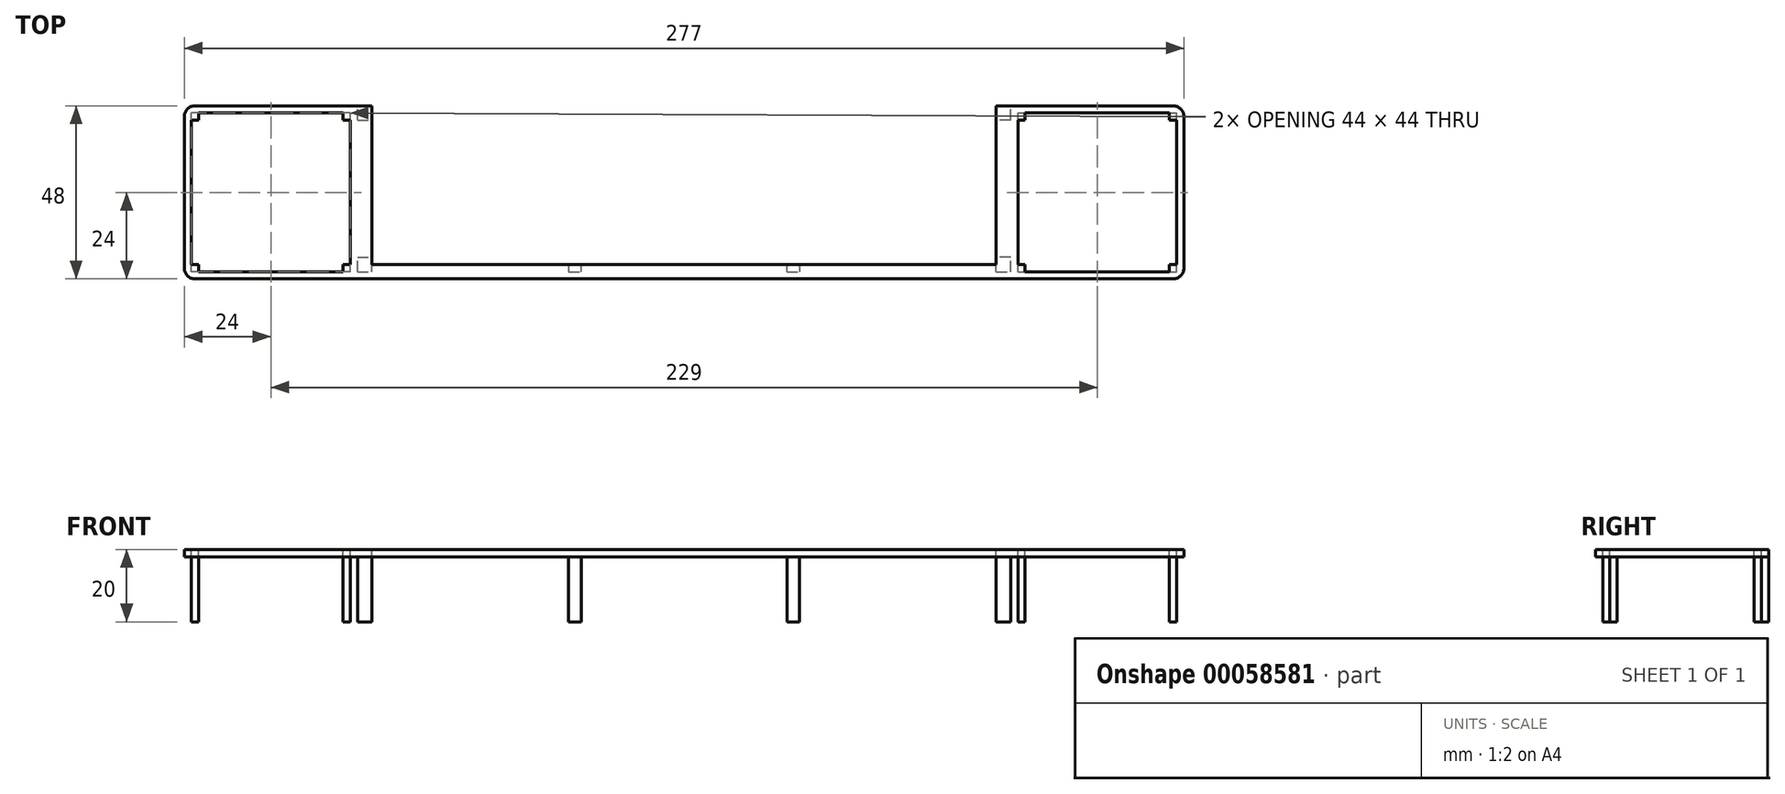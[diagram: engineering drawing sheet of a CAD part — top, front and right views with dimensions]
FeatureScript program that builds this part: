
annotation { "Feature Type Name" : "Feature", "Feature Type Description" : "" }
export const myFeature = defineFeature(function(context is Context, id is Id, definition is map)
    precondition{}
    {
        {
            var Q0;
            Q0=qCreatedBy(makeId("Top.planeOp"),FACE);
            var sketch = newSketch(context, id + "F0", { "sketchPlane" : qUnion([Q0])});
            skLineSegment(sketch, "E0", {"start": v(0, 42.64) * mm, "end": v(0, 0) * mm, "construction": true});
            skLineSegment(sketch, "E1", {"start": v(0, 0) * mm, "end": v(-90.5, 0) * mm, "construction": true});
            skLineSegment(sketch, "E2.bottom", {"start": v(-90.5, 0) * mm, "end": v(-138.5, 0) * mm});
            skLineSegment(sketch, "E2.top", {"start": v(-90.5, 48) * mm, "end": v(-138.5, 48) * mm});
            skLineSegment(sketch, "E2.left", {"start": v(-90.5, 2) * mm, "end": v(-90.5, 48) * mm});
            skLineSegment(sketch, "E2.right", {"start": v(-138.5, 0) * mm, "end": v(-138.5, 48) * mm});
            skLineSegment(sketch, "E3.0", {"start": v(-92.5, 46) * mm, "end": v(-136.5, 46) * mm});
            skLineSegment(sketch, "E3.1", {"start": v(-92.5, 2) * mm, "end": v(-92.5, 46) * mm});
            skLineSegment(sketch, "E3.2", {"start": v(-92.5, 2) * mm, "end": v(-136.5, 2) * mm});
            skLineSegment(sketch, "E3.3", {"start": v(-136.5, 2) * mm, "end": v(-136.5, 46) * mm});
            skLineSegment(sketch, "E4", {"start": v(-90.5, 0) * mm, "end": v(0, 0) * mm});
            skLineSegment(sketch, "E5", {"start": v(-90.5, 2) * mm, "end": v(0, 2) * mm});
            skLineSegment(sketch, "E6", {"start": v(0, 0) * mm, "end": v(0, 2) * mm});
            skSolve(sketch);
        }
        {
            var Q0;
            Q0 = qSketchRegion(id + "F0", true);
            extrude(context, id + "F1", {"entities" : qUnion([Q0]), "depth" : 17 * mm});
        }
        {
            var Q0;
            Q0=makeQuery(id+"F1.opExtrude","CAP_FACE",FACE,{"disambiguationData":[OSD([sQuery(id+"F0.wireOp",EDGE,"E2.bottom"),sQuery(id+"F0.wireOp",EDGE,"E2.top"),sQuery(id+"F0.wireOp",EDGE,"E2.left"),sQuery(id+"F0.wireOp",EDGE,"E2.right"),sQuery(id+"F0.wireOp",EDGE,"E3.0"),sQuery(id+"F0.wireOp",EDGE,"E3.1"),sQuery(id+"F0.wireOp",EDGE,"E3.2"),sQuery(id+"F0.wireOp",EDGE,"E3.3"),sQuery(id+"F0.wireOp",EDGE,"E4"),sQuery(id+"F0.wireOp",EDGE,"E5"),sQuery(id+"F0.wireOp",EDGE,"8706801c-66d0-493c-a020-fb1d76b9bbb51.MirrorCS"),sQuery(id+"F0.wireOp",EDGE,"8706801c-66d0-493c-a020-fb1d76b9bbb52.MirrorCS"),sQuery(id+"F0.wireOp",EDGE,"8706801c-66d0-493c-a020-fb1d76b9bbb53.MirrorCS"),sQuery(id+"F0.wireOp",EDGE,"8706801c-66d0-493c-a020-fb1d76b9bbb54.MirrorCS"),sQuery(id+"F0.wireOp",EDGE,"8706801c-66d0-493c-a020-fb1d76b9bbb55.MirrorCS"),sQuery(id+"F0.wireOp",EDGE,"8706801c-66d0-493c-a020-fb1d76b9bbb56.MirrorCS"),sQuery(id+"F0.wireOp",EDGE,"8706801c-66d0-493c-a020-fb1d76b9bbb57.MirrorCS"),sQuery(id+"F0.wireOp",EDGE,"8706801c-66d0-493c-a020-fb1d76b9bbb58.MirrorCS"),sQuery(id+"F0.wireOp",EDGE,"8706801c-66d0-493c-a020-fb1d76b9bbb59.MirrorCS"),sQuery(id+"F0.wireOp",EDGE,"8706801c-66d0-493c-a020-fb1d76b9bbb510.MirrorCS")])],"isStart":false});
            var sketch = newSketch(context, id + "F2", { "sketchPlane" : qUnion([Q0])});
            skLineSegment(sketch, "E7.bottom", {"start": v(-136.5, 2) * mm, "end": v(-134.5, 2) * mm});
            skLineSegment(sketch, "E7.top", {"start": v(-136.5, 4) * mm, "end": v(-134.5, 4) * mm});
            skLineSegment(sketch, "E7.left", {"start": v(-136.5, 2) * mm, "end": v(-136.5, 4) * mm});
            skLineSegment(sketch, "E7.right", {"start": v(-134.5, 2) * mm, "end": v(-134.5, 4) * mm});
            skLineSegment(sketch, "E8.bottom", {"start": v(-136.5, 46) * mm, "end": v(-134.5, 46) * mm});
            skLineSegment(sketch, "E8.top", {"start": v(-136.5, 44) * mm, "end": v(-134.5, 44) * mm});
            skLineSegment(sketch, "E8.left", {"start": v(-136.5, 46) * mm, "end": v(-136.5, 44) * mm});
            skLineSegment(sketch, "E8.right", {"start": v(-134.5, 46) * mm, "end": v(-134.5, 44) * mm});
            skLineSegment(sketch, "E9.bottom", {"start": v(-92.5, 2) * mm, "end": v(-94.5, 2) * mm});
            skLineSegment(sketch, "E9.top", {"start": v(-92.5, 4) * mm, "end": v(-94.5, 4) * mm});
            skLineSegment(sketch, "E9.left", {"start": v(-92.5, 2) * mm, "end": v(-92.5, 4) * mm});
            skLineSegment(sketch, "E9.right", {"start": v(-94.5, 2) * mm, "end": v(-94.5, 4) * mm});
            skLineSegment(sketch, "E10.bottom", {"start": v(-92.5, 46) * mm, "end": v(-94.5, 46) * mm});
            skLineSegment(sketch, "E10.top", {"start": v(-92.5, 44) * mm, "end": v(-94.5, 44) * mm});
            skLineSegment(sketch, "E10.left", {"start": v(-92.5, 46) * mm, "end": v(-92.5, 44) * mm});
            skLineSegment(sketch, "E10.right", {"start": v(-94.5, 46) * mm, "end": v(-94.5, 44) * mm});
            skLineSegment(sketch, "E11.bottom", {"start": v(-90.5, 48) * mm, "end": v(-86.5, 48) * mm});
            skLineSegment(sketch, "E11.top", {"start": v(-90.5, 44) * mm, "end": v(-86.5, 44) * mm});
            skLineSegment(sketch, "E11.left", {"start": v(-90.5, 48) * mm, "end": v(-90.5, 44) * mm});
            skLineSegment(sketch, "E11.right", {"start": v(-86.5, 48) * mm, "end": v(-86.5, 44) * mm});
            skLineSegment(sketch, "E12.bottom", {"start": v(-90.5, 2) * mm, "end": v(-86.5, 2) * mm});
            skLineSegment(sketch, "E12.top", {"start": v(-90.5, 6) * mm, "end": v(-86.5, 6) * mm});
            skLineSegment(sketch, "E12.left", {"start": v(-90.5, 2) * mm, "end": v(-90.5, 6) * mm});
            skLineSegment(sketch, "E12.right", {"start": v(-86.5, 2) * mm, "end": v(-86.5, 6) * mm});
            skLineSegment(sketch, "E13.bottom", {"start": v(-32, 2) * mm, "end": v(-28.5, 2) * mm});
            skLineSegment(sketch, "E14", {"start": v(-32, 2) * mm, "end": v(-32, 4) * mm});
            skLineSegment(sketch, "E15", {"start": v(-32, 4) * mm, "end": v(-28.5, 4) * mm});
            skLineSegment(sketch, "E16", {"start": v(-28.5, 4) * mm, "end": v(-28.5, 2) * mm});
            skSolve(sketch);
        }
        {
            var Q0;
            Q0 = qSketchRegion(id + "F2", true);
            extrude(context, id + "F3", {"entities" : qUnion([Q0]), "operationType" : NewBodyOperationType.ADD, "oppositeDirection" : true, "depth" : 20 * mm});
        }
        {
            var Q0;
            Q0=makeQuery(id+"F3.boolean.opBoolean","MERGE",FACE,{"derivedFrom":[makeQuery(id+"F1.opExtrude","CAP_FACE",FACE,{"disambiguationData":[OSD([sQuery(id+"F0.wireOp",EDGE,"E2.bottom"),sQuery(id+"F0.wireOp",EDGE,"E2.top"),sQuery(id+"F0.wireOp",EDGE,"E2.left"),sQuery(id+"F0.wireOp",EDGE,"E2.right"),sQuery(id+"F0.wireOp",EDGE,"E3.0"),sQuery(id+"F0.wireOp",EDGE,"E3.1"),sQuery(id+"F0.wireOp",EDGE,"E3.2"),sQuery(id+"F0.wireOp",EDGE,"E3.3"),sQuery(id+"F0.wireOp",EDGE,"E4"),sQuery(id+"F0.wireOp",EDGE,"E5"),sQuery(id+"F0.wireOp",EDGE,"E6")])],"isStart":false}),makeQuery(id+"F3.opExtrude","CAP_FACE",FACE,{"disambiguationData":[OSD([sQuery(id+"F2.wireOp",EDGE,"E7.bottom"),sQuery(id+"F2.wireOp",EDGE,"E7.top"),sQuery(id+"F2.wireOp",EDGE,"E7.left"),sQuery(id+"F2.wireOp",EDGE,"E7.right")])],"isStart":true}),makeQuery(id+"F3.opExtrude","CAP_FACE",FACE,{"disambiguationData":[OSD([sQuery(id+"F2.wireOp",EDGE,"E8.bottom"),sQuery(id+"F2.wireOp",EDGE,"E8.top"),sQuery(id+"F2.wireOp",EDGE,"E8.left"),sQuery(id+"F2.wireOp",EDGE,"E8.right")])],"isStart":true}),makeQuery(id+"F3.opExtrude","CAP_FACE",FACE,{"disambiguationData":[OSD([sQuery(id+"F2.wireOp",EDGE,"E9.bottom"),sQuery(id+"F2.wireOp",EDGE,"E9.top"),sQuery(id+"F2.wireOp",EDGE,"E9.left"),sQuery(id+"F2.wireOp",EDGE,"E9.right")])],"isStart":true}),makeQuery(id+"F3.opExtrude","CAP_FACE",FACE,{"disambiguationData":[OSD([sQuery(id+"F2.wireOp",EDGE,"E10.bottom"),sQuery(id+"F2.wireOp",EDGE,"E10.top"),sQuery(id+"F2.wireOp",EDGE,"E10.left"),sQuery(id+"F2.wireOp",EDGE,"E10.right")])],"isStart":true}),makeQuery(id+"F3.opExtrude","CAP_FACE",FACE,{"disambiguationData":[OSD([sQuery(id+"F2.wireOp",EDGE,"E11.bottom"),sQuery(id+"F2.wireOp",EDGE,"E11.top"),sQuery(id+"F2.wireOp",EDGE,"E11.left"),sQuery(id+"F2.wireOp",EDGE,"E11.right")])],"isStart":true}),makeQuery(id+"F3.opExtrude","CAP_FACE",FACE,{"disambiguationData":[OSD([sQuery(id+"F2.wireOp",EDGE,"E12.bottom"),sQuery(id+"F2.wireOp",EDGE,"E12.top"),sQuery(id+"F2.wireOp",EDGE,"E12.left"),sQuery(id+"F2.wireOp",EDGE,"E12.right")])],"isStart":true}),makeQuery(id+"F3.opExtrude","CAP_FACE",FACE,{"disambiguationData":[OSD([sQuery(id+"F2.wireOp",EDGE,"E13.bottom"),sQuery(id+"F2.wireOp",EDGE,"E14"),sQuery(id+"F2.wireOp",EDGE,"E15"),sQuery(id+"F2.wireOp",EDGE,"E16")])],"isStart":true})]});
            var sketch = newSketch(context, id + "F4", { "sketchPlane" : qUnion([Q0])});
            skLineSegment(sketch, "E17.bottom", {"start": v(-86.5, 44) * mm, "end": v(-90.5, 44) * mm});
            skLineSegment(sketch, "E17.top", {"start": v(-86.5, 6) * mm, "end": v(-90.5, 6) * mm});
            skLineSegment(sketch, "E17.left", {"start": v(-86.5, 44) * mm, "end": v(-86.5, 6) * mm});
            skLineSegment(sketch, "E17.right", {"start": v(-90.5, 44) * mm, "end": v(-90.5, 6) * mm});
            skLineSegment(sketch, "E18.bottom", {"start": v(-86.5, 2) * mm, "end": v(0, 2) * mm});
            skLineSegment(sketch, "E18.top", {"start": v(-86.5, 4) * mm, "end": v(0, 4) * mm});
            skLineSegment(sketch, "E18.left", {"start": v(-86.5, 2) * mm, "end": v(-86.5, 4) * mm});
            skLineSegment(sketch, "E18.right", {"start": v(0, 2) * mm, "end": v(0, 4) * mm});
            skSolve(sketch);
        }
        {
            var Q0;
            Q0 = qSketchRegion(id + "F4", true);
            extrude(context, id + "F5", {"entities" : qUnion([Q0]), "operationType" : NewBodyOperationType.ADD, "oppositeDirection" : true, "depth" : 2 * mm});
        }
        {
            var Q0;
            Q0=makeQuery(id+"F1.opExtrude","SWEPT_BODY",BODY,{"disambiguationData":[OSD([sQuery(id+"F0.wireOp",EDGE,"E2.bottom"),sQuery(id+"F0.wireOp",EDGE,"E2.top"),sQuery(id+"F0.wireOp",EDGE,"E2.left"),sQuery(id+"F0.wireOp",EDGE,"E2.right"),sQuery(id+"F0.wireOp",EDGE,"E3.0"),sQuery(id+"F0.wireOp",EDGE,"E3.1"),sQuery(id+"F0.wireOp",EDGE,"E3.2"),sQuery(id+"F0.wireOp",EDGE,"E3.3"),sQuery(id+"F0.wireOp",EDGE,"E4"),sQuery(id+"F0.wireOp",EDGE,"E5"),sQuery(id+"F0.wireOp",EDGE,"E6")])]});
            var Q1;
            Q1=makeQuery(id+"F1.opExtrude","SWEPT_FACE",FACE,{"disambiguationData":[OSD([sQuery(id+"F0.wireOp",EDGE,"E6")])]});
            mirror(context, id + "F6", {"operationType" : NewBodyOperationType.ADD, "entities" : qUnion([Q0]), "mirrorPlane" : qUnion([Q1])});
        }
        {
            var Q0;
            Q0=makeQuery(id+"F1.opExtrude","SWEPT_EDGE",EDGE,{"disambiguationData":[OSD([sQuery(id+"F0.wireOp",EDGE,"E2.bottom"),sQuery(id+"F0.wireOp",EDGE,"E2.right")])]});
            var Q1;
            Q1=makeQuery(id+"F6.opPattern","COPY",EDGE,{"derivedFrom":makeQuery(id+"F1.opExtrude","SWEPT_EDGE",EDGE,{"disambiguationData":[OSD([sQuery(id+"F0.wireOp",EDGE,"E2.bottom"),sQuery(id+"F0.wireOp",EDGE,"E2.right")])]}),"instanceName":"1"});
            fillet(context, id + "F7", {"entities" : qUnion([Q0, Q1]), "radius" : 3 * mm, "tangentPropagation" : true, "allowEdgeOverflow" : false});
        }
        {
            var Q0;
            Q0=makeQuery(id+"F1.opExtrude","SWEPT_EDGE",EDGE,{"disambiguationData":[OSD([sQuery(id+"F0.wireOp",EDGE,"E2.top"),sQuery(id+"F0.wireOp",EDGE,"E2.right")])]});
            var Q1;
            Q1=makeQuery(id+"F6.opPattern","COPY",EDGE,{"derivedFrom":makeQuery(id+"F1.opExtrude","SWEPT_EDGE",EDGE,{"disambiguationData":[OSD([sQuery(id+"F0.wireOp",EDGE,"E2.top"),sQuery(id+"F0.wireOp",EDGE,"E2.right")])]}),"instanceName":"1"});
            fillet(context, id + "F8", {"entities" : qUnion([Q0, Q1]), "radius" : 3 * mm, "tangentPropagation" : true, "allowEdgeOverflow" : false});
        }
        {
            var Q0;
            {var subQ0=makeQuery(id+"F1.opExtrude","CAP_FACE",FACE,{"disambiguationData":[OSD([sQuery(id+"F0.wireOp",EDGE,"E2.bottom"),sQuery(id+"F0.wireOp",EDGE,"E2.top"),sQuery(id+"F0.wireOp",EDGE,"E2.left"),sQuery(id+"F0.wireOp",EDGE,"E2.right"),sQuery(id+"F0.wireOp",EDGE,"E3.0"),sQuery(id+"F0.wireOp",EDGE,"E3.1"),sQuery(id+"F0.wireOp",EDGE,"E3.2"),sQuery(id+"F0.wireOp",EDGE,"E3.3"),sQuery(id+"F0.wireOp",EDGE,"E4"),sQuery(id+"F0.wireOp",EDGE,"E5"),sQuery(id+"F0.wireOp",EDGE,"E6")])],"isStart":true});Q0=makeQuery(id+"F6.boolean.opBoolean","MERGE",FACE,{"derivedFrom":[subQ0,makeQuery(id+"F6.opPattern","COPY",FACE,{"derivedFrom":subQ0,"instanceName":"1"})]});}
            extrude(context, id + "F9", {"entities" : qUnion([Q0]), "operationType" : NewBodyOperationType.REMOVE, "oppositeDirection" : true, "depth" : 15 * mm});
        }
    });
